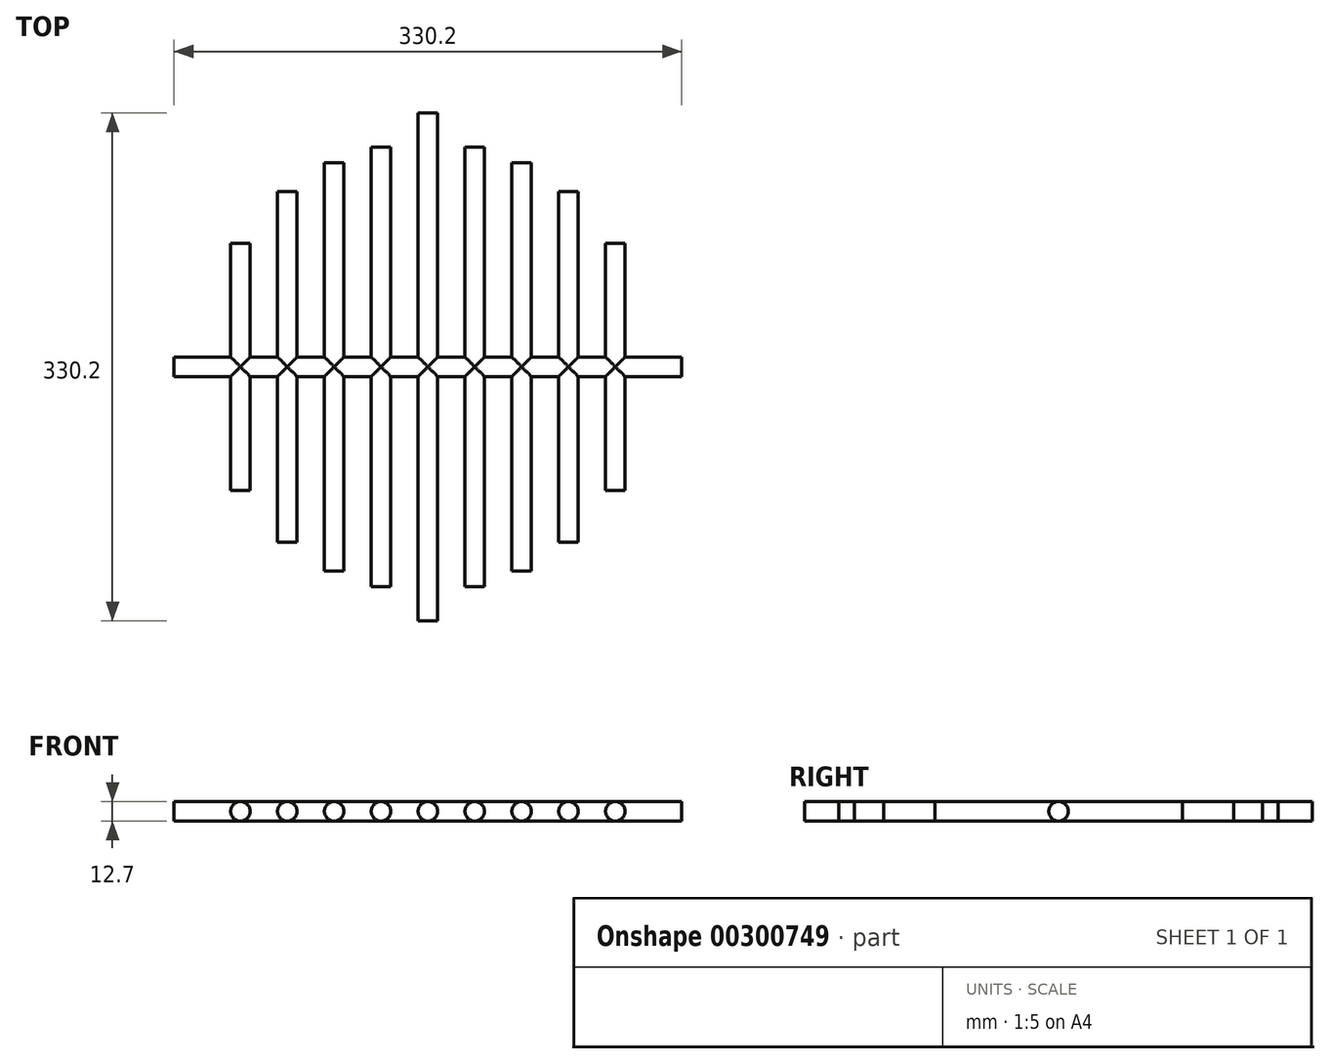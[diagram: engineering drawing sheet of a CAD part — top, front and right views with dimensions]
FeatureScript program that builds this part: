
annotation { "Feature Type Name" : "Feature", "Feature Type Description" : "" }
export const myFeature = defineFeature(function(context is Context, id is Id, definition is map)
    precondition{}
    {
        {
            var Q0;
            Q0=qCreatedBy(makeId("Top.planeOp"),FACE);
            var sketch = newSketch(context, id + "F0", { "sketchPlane" : qUnion([Q0])});
            skCircle(sketch, "E0", {"center": v(0, 0) * mm, "radius": 146.05 * mm, "construction": true});
            skCircle(sketch, "E1", {"center": v(0, 0) * mm, "radius": 165.1 * mm, "construction": true});
            skLineSegment(sketch, "E2", {"start": v(0, -165.1) * mm, "end": v(0, 165.1) * mm});
            skLineSegment(sketch, "E3", {"start": v(-165.1, 0) * mm, "end": v(165.1, 0) * mm});
            skLineSegment(sketch, "E4", {"start": v(-30.48, -142.83) * mm, "end": v(-30.48, 142.83) * mm});
            skLineSegment(sketch, "E5", {"start": v(-60.96, -132.72) * mm, "end": v(-60.96, 132.72) * mm});
            skLineSegment(sketch, "E6", {"start": v(-91.44, -113.88) * mm, "end": v(-91.44, 113.88) * mm});
            skLineSegment(sketch, "E7", {"start": v(-121.92, -80.41) * mm, "end": v(-121.92, 80.41) * mm});
            skLineSegment(sketch, "E8.MirrorCS", {"start": v(30.48, -142.83) * mm, "end": v(30.48, 142.83) * mm});
            skLineSegment(sketch, "E9.MirrorCS", {"start": v(60.96, -132.72) * mm, "end": v(60.96, 132.72) * mm});
            skLineSegment(sketch, "E10.MirrorCS", {"start": v(91.44, -113.88) * mm, "end": v(91.44, 113.88) * mm});
            skLineSegment(sketch, "E11.MirrorCS", {"start": v(121.92, -80.41) * mm, "end": v(121.92, 80.41) * mm});
            skSolve(sketch);
        }
        {
            var Q0;
            Q0=sQuery(id+"F0.wireOp",VERTEX,"E2.start");
            var Q1;
            Q1=qCreatedBy(makeId("Front.planeOp"),FACE);
            cPlane(context, id + "F1", {"entities" : qUnion([Q0, Q1]), "cplaneType" : CPlaneType.PLANE_POINT, "offset" : 25.4 * mm, "width" : 152.4 * mm, "height" : 152.4 * mm});
        }
        {
            var Q0;
            Q0=sQuery(id+"F0.wireOp",VERTEX,"E2.end");
            var Q1;
            Q1=qCreatedBy(makeId("Front.planeOp"),FACE);
            cPlane(context, id + "F2", {"entities" : qUnion([Q0, Q1]), "cplaneType" : CPlaneType.PLANE_POINT, "offset" : 25.4 * mm, "width" : 152.4 * mm, "height" : 152.4 * mm});
        }
        {
            var Q0;
            Q0=qCreatedBy(id+"F2.planeOp",FACE);
            var sketch = newSketch(context, id + "F3", { "sketchPlane" : qUnion([Q0])});
            skCircle(sketch, "E12", {"center": v(0, 0) * mm, "radius": 6.35 * mm});
            skSolve(sketch);
        }
        {
            var Q0;
            Q0=makeQuery(id+"F3.imprint","IMPRINT",FACE,{"disambiguationData":[TD([[makeQuery(id+"F3.imprint","IMPRINT",EDGE,{"derivedFrom":sQuery(id+"F3.wireOp",EDGE,"E12")}),1.0]])]});
            var Q1;
            Q1=sQuery(id+"F0.wireOp",EDGE,"E2");
            sweep(context, id + "F4", {"profiles" : qUnion([Q0]), "path" : qUnion([Q1])});
        }
        {
            var Q0;
            Q0=sQuery(id+"F0.wireOp",VERTEX,"E3.end");
            var Q1;
            Q1=qCreatedBy(makeId("Right.planeOp"),FACE);
            cPlane(context, id + "F5", {"entities" : qUnion([Q0, Q1]), "cplaneType" : CPlaneType.PLANE_POINT, "offset" : 25.4 * mm, "width" : 152.4 * mm, "height" : 152.4 * mm});
        }
        {
            var Q0;
            Q0=qCreatedBy(id+"F5.planeOp",FACE);
            var sketch = newSketch(context, id + "F6", { "sketchPlane" : qUnion([Q0])});
            skCircle(sketch, "E13", {"center": v(0, 0) * mm, "radius": 6.35 * mm});
            skSolve(sketch);
        }
        {
            var Q0;
            Q0=makeQuery(id+"F6.imprint","IMPRINT",FACE,{"disambiguationData":[TD([[makeQuery(id+"F6.imprint","IMPRINT",EDGE,{"derivedFrom":sQuery(id+"F6.wireOp",EDGE,"E13")}),1.0]])]});
            var Q1;
            Q1=sQuery(id+"F0.wireOp",EDGE,"E3");
            sweep(context, id + "F7", {"operationType" : NewBodyOperationType.ADD, "profiles" : qUnion([Q0]), "path" : qUnion([Q1])});
        }
        {
            var Q0;
            Q0=sQuery(id+"F0.wireOp",VERTEX,"E8.MirrorCS.start");
            var Q1;
            Q1=qCreatedBy(makeId("Front.planeOp"),FACE);
            cPlane(context, id + "F8", {"entities" : qUnion([Q0, Q1]), "cplaneType" : CPlaneType.PLANE_POINT, "offset" : 25.4 * mm, "width" : 152.4 * mm, "height" : 152.4 * mm});
        }
        {
            var Q0;
            Q0=qCreatedBy(id+"F8.planeOp",FACE);
            var sketch = newSketch(context, id + "F9", { "sketchPlane" : qUnion([Q0])});
            skCircle(sketch, "E14", {"center": v(30.48, 0) * mm, "radius": 6.35 * mm});
            skSolve(sketch);
        }
        {
            var Q0;
            Q0=makeQuery(id+"F9.imprint","IMPRINT",FACE,{"disambiguationData":[TD([[makeQuery(id+"F9.imprint","IMPRINT",EDGE,{"derivedFrom":sQuery(id+"F9.wireOp",EDGE,"E14")}),1.0]])]});
            var Q1;
            Q1=sQuery(id+"F0.wireOp",EDGE,"E8.MirrorCS");
            sweep(context, id + "F10", {"operationType" : NewBodyOperationType.ADD, "profiles" : qUnion([Q0]), "path" : qUnion([Q1])});
        }
        {
            var Q0;
            Q0=sQuery(id+"F0.wireOp",VERTEX,"E9.MirrorCS.start");
            var Q1;
            Q1=qCreatedBy(makeId("Front.planeOp"),FACE);
            cPlane(context, id + "F11", {"entities" : qUnion([Q0, Q1]), "cplaneType" : CPlaneType.PLANE_POINT, "offset" : 25.4 * mm, "width" : 152.4 * mm, "height" : 152.4 * mm});
        }
        {
            var Q0;
            Q0=qCreatedBy(id+"F11.planeOp",FACE);
            var sketch = newSketch(context, id + "F12", { "sketchPlane" : qUnion([Q0])});
            skCircle(sketch, "E15", {"center": v(60.96, 0) * mm, "radius": 6.35 * mm});
            skSolve(sketch);
        }
        {
            var Q0;
            Q0=makeQuery(id+"F12.imprint","IMPRINT",FACE,{"disambiguationData":[TD([[makeQuery(id+"F12.imprint","IMPRINT",EDGE,{"derivedFrom":sQuery(id+"F12.wireOp",EDGE,"E15")}),1.0]])]});
            var Q1;
            Q1=sQuery(id+"F0.wireOp",EDGE,"E9.MirrorCS");
            sweep(context, id + "F13", {"operationType" : NewBodyOperationType.ADD, "profiles" : qUnion([Q0]), "path" : qUnion([Q1])});
        }
        {
            var Q0;
            Q0=sQuery(id+"F0.wireOp",VERTEX,"E10.MirrorCS.start");
            var Q1;
            Q1=qCreatedBy(makeId("Front.planeOp"),FACE);
            cPlane(context, id + "F14", {"entities" : qUnion([Q0, Q1]), "cplaneType" : CPlaneType.PLANE_POINT, "offset" : 25.4 * mm, "width" : 152.4 * mm, "height" : 152.4 * mm});
        }
        {
            var Q0;
            Q0=qCreatedBy(id+"F14.planeOp",FACE);
            var sketch = newSketch(context, id + "F15", { "sketchPlane" : qUnion([Q0])});
            skCircle(sketch, "E16", {"center": v(91.44, 0) * mm, "radius": 6.35 * mm});
            skSolve(sketch);
        }
        {
            var Q0;
            Q0=makeQuery(id+"F15.imprint","IMPRINT",FACE,{"disambiguationData":[TD([[makeQuery(id+"F15.imprint","IMPRINT",EDGE,{"derivedFrom":sQuery(id+"F15.wireOp",EDGE,"E16")}),1.0]])]});
            var Q1;
            Q1=sQuery(id+"F0.wireOp",EDGE,"E10.MirrorCS");
            sweep(context, id + "F16", {"operationType" : NewBodyOperationType.ADD, "profiles" : qUnion([Q0]), "path" : qUnion([Q1])});
        }
        {
            var Q0;
            Q0=sQuery(id+"F0.wireOp",VERTEX,"E11.MirrorCS.start");
            var Q1;
            Q1=qCreatedBy(makeId("Front.planeOp"),FACE);
            cPlane(context, id + "F17", {"entities" : qUnion([Q0, Q1]), "cplaneType" : CPlaneType.PLANE_POINT, "offset" : 25.4 * mm, "width" : 152.4 * mm, "height" : 152.4 * mm});
        }
        {
            var Q0;
            Q0=qCreatedBy(id+"F17.planeOp",FACE);
            var sketch = newSketch(context, id + "F18", { "sketchPlane" : qUnion([Q0])});
            skCircle(sketch, "E17", {"center": v(121.92, 0) * mm, "radius": 6.35 * mm});
            skSolve(sketch);
        }
        {
            var Q0;
            Q0=makeQuery(id+"F18.imprint","IMPRINT",FACE,{"disambiguationData":[TD([[makeQuery(id+"F18.imprint","IMPRINT",EDGE,{"derivedFrom":sQuery(id+"F18.wireOp",EDGE,"E17")}),1.0]])]});
            var Q1;
            Q1=sQuery(id+"F0.wireOp",EDGE,"E11.MirrorCS");
            sweep(context, id + "F19", {"operationType" : NewBodyOperationType.ADD, "profiles" : qUnion([Q0]), "path" : qUnion([Q1])});
        }
        {
            var Q0;
            Q0=makeQuery(id+"F4.opSweep","SWEPT_BODY",BODY,{"disambiguationData":[OSD([sQuery(id+"F0.wireOp",EDGE,"E2"),sQuery(id+"F3.wireOp",EDGE,"E12")])]});
            var Q1;
            Q1=qCreatedBy(makeId("Right.planeOp"),FACE);
            mirror(context, id + "F20", {"operationType" : NewBodyOperationType.ADD, "entities" : qUnion([Q0]), "mirrorPlane" : qUnion([Q1])});
        }
    });
